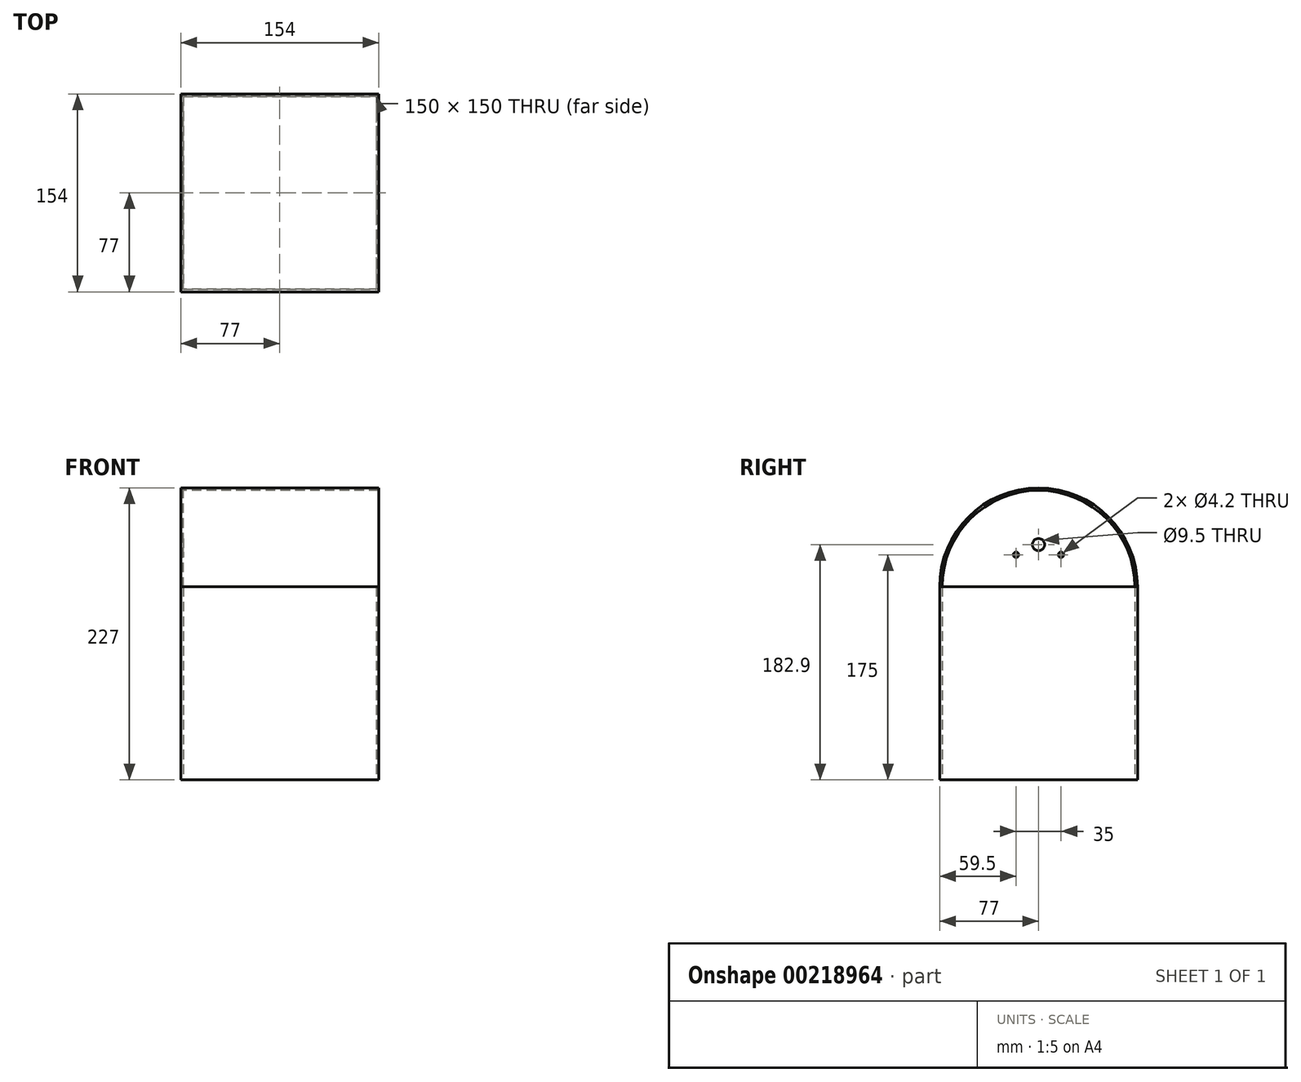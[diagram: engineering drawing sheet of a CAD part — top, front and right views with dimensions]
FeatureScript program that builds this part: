
annotation { "Feature Type Name" : "Feature", "Feature Type Description" : "" }
export const myFeature = defineFeature(function(context is Context, id is Id, definition is map)
    precondition{}
    {
        {
            assignVariable(context, id + "F0", {"name" : "wall", "anyValue" : 2});
        }
        {
            assignVariable(context, id + "F1", {"name" : "box", "anyValue" : 150});
        }
        {
            var Q0;
            Q0=qCreatedBy(makeId("Top.planeOp"),FACE);
            var sketch = newSketch(context, id + "F2", { "sketchPlane" : qUnion([Q0])});
            skLineSegment(sketch, "E0.bottom", {"start": v(-175, 125) * mm, "end": v(175, 125) * mm, "construction": true});
            skLineSegment(sketch, "E0.top", {"start": v(-175, -125) * mm, "end": v(175, -125) * mm, "construction": true});
            skLineSegment(sketch, "E0.left", {"start": v(-175, 125) * mm, "end": v(-175, -125) * mm, "construction": true});
            skLineSegment(sketch, "E0.right", {"start": v(175, 125) * mm, "end": v(175, -125) * mm, "construction": true});
            skPoint(sketch, "E0.middle", {"position": v(0, 0) * mm});
            skLineSegment(sketch, "E1.bottom", {"start": v(-75, 75) * mm, "end": v(75, 75) * mm});
            skLineSegment(sketch, "E1.top", {"start": v(-75, -75) * mm, "end": v(75, -75) * mm});
            skLineSegment(sketch, "E1.left", {"start": v(-75, 75) * mm, "end": v(-75, -75) * mm});
            skLineSegment(sketch, "E1.right", {"start": v(75, 75) * mm, "end": v(75, -75) * mm});
            skLineSegment(sketch, "E2.0", {"start": v(-77, 77) * mm, "end": v(77, 77) * mm});
            skLineSegment(sketch, "E2.1", {"start": v(-77, 77) * mm, "end": v(-77, -77) * mm});
            skLineSegment(sketch, "E2.2", {"start": v(-77, -77) * mm, "end": v(77, -77) * mm});
            skLineSegment(sketch, "E2.3", {"start": v(77, 77) * mm, "end": v(77, -77) * mm});
            skSolve(sketch);
        }
        {
            var Q0;
            Q0=makeQuery(id+"F2.imprint","IMPRINT",FACE,{"disambiguationData":[TD([[makeQuery(id+"F2.imprint","IMPRINT",EDGE,{"derivedFrom":sQuery(id+"F2.wireOp",EDGE,"E1.bottom")}),1.0]])]});
            extrude(context, id + "F3", {"entities" : qUnion([Q0]), "depth" : (getVariable(context, 'box')) * mm});
        }
        {
            var Q0;
            Q0=makeQuery(id+"F3.opExtrude","SWEPT_FACE",FACE,{"disambiguationData":[OSD([sQuery(id+"F2.wireOp",EDGE,"E2.1")])]});
            var sketch = newSketch(context, id + "F4", { "sketchPlane" : qUnion([Q0])});
            skLineSegment(sketch, "E3.0", {"start": v(-77, 150) * mm, "end": v(77, 150) * mm});
            skCircle(sketch, "E4", {"center": v(0, 150) * mm, "radius": 75 * mm});
            skCircle(sketch, "E5.0", {"center": v(0, 150) * mm, "radius": 77 * mm});
            skCircle(sketch, "E6", {"center": v(0, 182.9) * mm, "radius": 4.75 * mm});
            skLineSegment(sketch, "E7", {"start": v(0, 182.9) * mm, "end": v(0, 175) * mm, "construction": true});
            skLineSegment(sketch, "E8", {"start": v(-17.5, 175) * mm, "end": v(17.5, 175) * mm, "construction": true});
            skPoint(sketch, "E9", {"position": v(0, 175) * mm});
            skCircle(sketch, "E10", {"center": v(-17.5, 175) * mm, "radius": 2.1 * mm});
            skCircle(sketch, "E11.MirrorC", {"center": v(17.5, 175) * mm, "radius": 2.1 * mm});
            skSolve(sketch);
        }
        {
            var Q0;
            {var subQ2=sQuery(id+"F2.wireOp",EDGE,"E2.1");var subQ3=makeQuery(id+"F3.opExtrude","SWEPT_EDGE",EDGE,{"disambiguationData":[OSD([sQuery(id+"F2.wireOp",EDGE,"E2.0"),subQ2])]});var subQ7=sQuery(id+"F4.wireOp",EDGE,"E5.0");var subQ9=makeQuery(id+"F4.imprint","INTERSECT",VERTEX,{"derivedFrom":[subQ3,subQ7]});Q0=makeQuery(id+"F4.imprint","IMPRINT",FACE,{"disambiguationData":[TD([[makeQuery(id+"F4.imprint","IMPRINT",EDGE,{"disambiguationData":[TD([[subQ9,1.0]])],"derivedFrom":subQ7}),1.0]])]});}
            extrude(context, id + "F5", {"entities" : qUnion([Q0]), "oppositeDirection" : true, "depth" : (getVariable(context, 'box') + (2 * getVariable(context, 'wall'))) * mm});
        }
        {
            var Q0;
            {var subQ0=sQuery(id+"F4.wireOp",EDGE,"E4");var subQ1=sQuery(id+"F4.wireOp",EDGE,"E3.0");var subQ2=makeQuery(id+"F4.imprint","INTERSECT",VERTEX,{"disambiguationData":[OD(0.0)],"derivedFrom":[subQ1,subQ0]});Q0=makeQuery(id+"F4.imprint","IMPRINT",FACE,{"disambiguationData":[TD([[makeQuery(id+"F4.imprint","IMPRINT",EDGE,{"disambiguationData":[TD([[subQ2,-1.0]])],"derivedFrom":subQ1}),1.0]])]});}
            extrude(context, id + "F6", {"entities" : qUnion([Q0]), "oppositeDirection" : true, "depth" : (getVariable(context, 'wall')) * mm});
        }
    });
